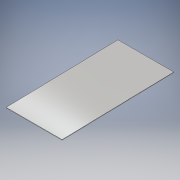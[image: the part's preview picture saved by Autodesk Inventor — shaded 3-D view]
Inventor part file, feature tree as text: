
AUTODESK INVENTOR PART (.ipt)
format: ipt  version: 2017 (Build 210142000, 142)  size: 170,496 bytes
history: native  units: in
note: dims shown in document units (in); Inventor stores cm internally (conversion verified against a paired STEP export)
features: sketch x3, extrude x2, mirror x1
ambient origin geometry x8: Origin, YZ Plane, XZ Plane, XY Plane, X Axis, Y Axis, Z Axis, Center Point
bodies: Solid1 (feature_tree)
feature tree (6):
  extrude  "Extrusion1"  Depth=202.0in
  extrude  "Extrusion2"  Depth=1.0in
  sketch  "Sketch3"  dims[d4=0.0in d5=101.0in d6=0.0in d7=20.1012in d8=20.1012in d9=20.1012in d10=20.1012in d11=2.0in d12=2.0in d13=2.0in d14=101.0in d15=2.0in d16=1.0in d17=0.25in d18=0.0in]
  mirror  "Mirror1"
  sketch  "Sketch1"  dims[d0=7.0in d1=202.0in]
  sketch  "Sketch2"  dims[d2=5.0in d3=1.0in]
